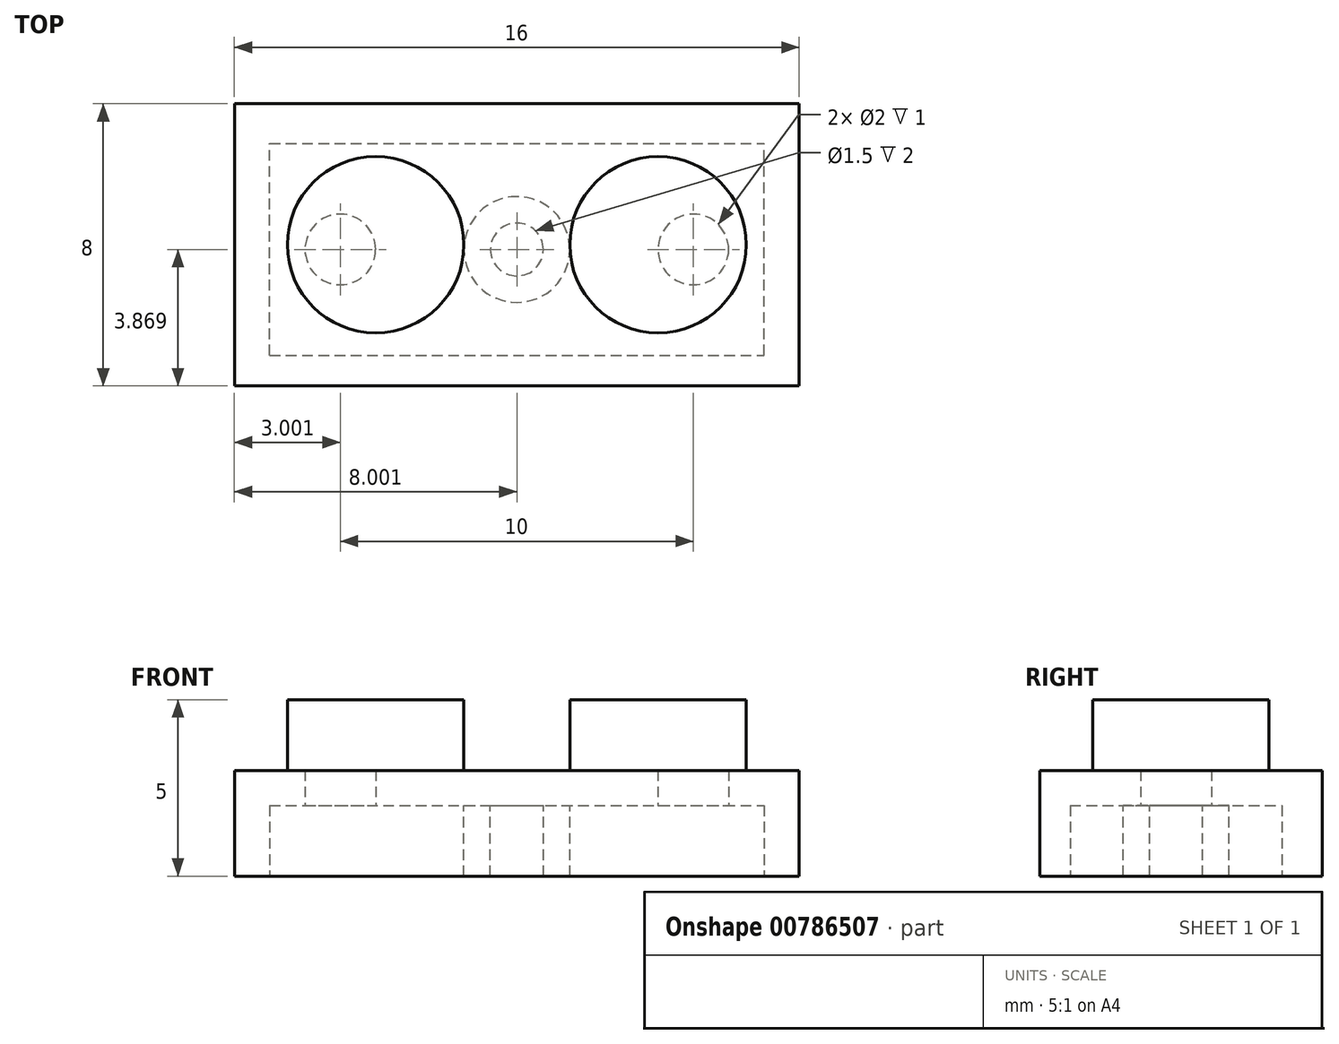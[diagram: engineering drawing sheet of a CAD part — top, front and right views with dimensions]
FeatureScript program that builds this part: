
annotation { "Feature Type Name" : "Feature", "Feature Type Description" : "" }
export const myFeature = defineFeature(function(context is Context, id is Id, definition is map)
    precondition{}
    {
        {
            var Q0;
            Q0=qCreatedBy(makeId("Top.planeOp"),FACE);
            var sketch = newSketch(context, id + "F0", { "sketchPlane" : qUnion([Q0])});
            skLineSegment(sketch, "E0.bottom", {"start": v(9.17, -1.05) * mm, "end": v(25.17, -1.05) * mm});
            skLineSegment(sketch, "E0.top", {"start": v(9.17, -9.05) * mm, "end": v(25.17, -9.05) * mm});
            skLineSegment(sketch, "E0.left", {"start": v(9.17, -1.05) * mm, "end": v(9.17, -9.05) * mm});
            skLineSegment(sketch, "E0.right", {"start": v(25.17, -1.05) * mm, "end": v(25.17, -9.05) * mm});
            skSolve(sketch);
        }
        {
            var Q0;
            Q0 = qSketchRegion(id + "F0", true);
            extrude(context, id + "F1", {"entities" : qUnion([Q0]), "depth" : 3 * mm, "offsetDistance" : 25 * mm});
        }
        {
            var Q0;
            Q0=makeQuery(id+"F1.opExtrude","CAP_FACE",FACE,{"disambiguationData":[OSD([sQuery(id+"F0.wireOp",EDGE,"E0.bottom"),sQuery(id+"F0.wireOp",EDGE,"E0.top"),sQuery(id+"F0.wireOp",EDGE,"E0.left"),sQuery(id+"F0.wireOp",EDGE,"E0.right")])],"isStart":false});
            var sketch = newSketch(context, id + "F2", { "sketchPlane" : qUnion([Q0])});
            skCircle(sketch, "E1", {"center": v(13.17, -5.05) * mm, "radius": 2.5 * mm});
            skCircle(sketch, "E2", {"center": v(21.17, -5.05) * mm, "radius": 2.5 * mm});
            skSolve(sketch);
        }
        {
            var Q0;
            Q0 = qSketchRegion(id + "F2", true);
            extrude(context, id + "F3", {"entities" : qUnion([Q0]), "operationType" : NewBodyOperationType.ADD, "depth" : 2 * mm, "offsetDistance" : 25 * mm});
        }
        {
            var Q0;
            Q0=makeQuery(id+"F1.opExtrude","CAP_FACE",FACE,{"disambiguationData":[OSD([sQuery(id+"F0.wireOp",EDGE,"E0.bottom"),sQuery(id+"F0.wireOp",EDGE,"E0.top"),sQuery(id+"F0.wireOp",EDGE,"E0.left"),sQuery(id+"F0.wireOp",EDGE,"E0.right")])],"isStart":true});
            var sketch = newSketch(context, id + "F4", { "sketchPlane" : qUnion([Q0])});
            skLineSegment(sketch, "E3.bottom", {"start": v(10.17, 8.18) * mm, "end": v(24.17, 8.18) * mm});
            skLineSegment(sketch, "E3.top", {"start": v(10.17, 2.18) * mm, "end": v(24.17, 2.18) * mm});
            skLineSegment(sketch, "E3.left", {"start": v(10.17, 8.18) * mm, "end": v(10.17, 2.18) * mm});
            skLineSegment(sketch, "E3.right", {"start": v(24.17, 8.18) * mm, "end": v(24.17, 2.18) * mm});
            skSolve(sketch);
        }
        {
            var Q0;
            Q0 = qSketchRegion(id + "F4", true);
            extrude(context, id + "F5", {"entities" : qUnion([Q0]), "operationType" : NewBodyOperationType.REMOVE, "oppositeDirection" : true, "depth" : 2 * mm, "offsetDistance" : 25 * mm});
        }
        {
            var Q0;
            Q0=makeQuery(id+"F5.boolean.opBoolean","COPY",FACE,{"derivedFrom":makeQuery(id+"F5.opExtrude","CAP_FACE",FACE,{"disambiguationData":[OSD([sQuery(id+"F4.wireOp",EDGE,"E3.bottom"),sQuery(id+"F4.wireOp",EDGE,"E3.top"),sQuery(id+"F4.wireOp",EDGE,"E3.left"),sQuery(id+"F4.wireOp",EDGE,"E3.right")])],"isStart":false})});
            var sketch = newSketch(context, id + "F6", { "sketchPlane" : qUnion([Q0])});
            skCircle(sketch, "E4", {"center": v(17.17, 5.18) * mm, "radius": 0.75 * mm});
            skPoint(sketch, "E4.centerSnap0", {"position": v(17.17, 8.18) * mm});
            skPoint(sketch, "E4.centerSnap1", {"position": v(24.17, 5.18) * mm});
            skCircle(sketch, "E5", {"center": v(17.17, 5.18) * mm, "radius": 1.5 * mm});
            skSolve(sketch);
        }
        {
            var Q0;
            Q0 = qSketchRegion(id + "F6", true);
            extrude(context, id + "F7", {"entities" : qUnion([Q0]), "operationType" : NewBodyOperationType.ADD, "depth" : 2 * mm, "offsetDistance" : 25 * mm});
        }
        {
            var Q0;
            {var subQ0=sQuery(id+"F4.wireOp",EDGE,"E3.right");var subQ1=sQuery(id+"F4.wireOp",EDGE,"E3.left");var subQ2=sQuery(id+"F4.wireOp",EDGE,"E3.top");var subQ3=sQuery(id+"F4.wireOp",EDGE,"E3.bottom");Q0=makeQuery(id+"F7.boolean.opBoolean","SPLIT",FACE,{"disambiguationData":[TD([makeQuery(id+"F5.boolean.opBoolean","COPY",FACE,{"derivedFrom":makeQuery(id+"F5.opExtrude","SWEPT_FACE",FACE,{"disambiguationData":[OSD([subQ3])]})})])],"derivedFrom":makeQuery(id+"F5.boolean.opBoolean","COPY",FACE,{"derivedFrom":makeQuery(id+"F5.opExtrude","CAP_FACE",FACE,{"disambiguationData":[OSD([subQ3,subQ2,subQ1,subQ0])],"isStart":false})})});}
            var sketch = newSketch(context, id + "F8", { "sketchPlane" : qUnion([Q0])});
            skCircle(sketch, "E6", {"center": v(12.17, 5.18) * mm, "radius": 1 * mm});
            skPoint(sketch, "E6.centerSnap0", {"position": v(10.17, 5.18) * mm});
            skCircle(sketch, "E7", {"center": v(22.17, 5.18) * mm, "radius": 1 * mm});
            skPoint(sketch, "E7.centerSnap0", {"position": v(24.17, 5.18) * mm});
            skSolve(sketch);
        }
        {
            var Q0;
            Q0 = qSketchRegion(id + "F8", true);
            extrude(context, id + "F9", {"entities" : qUnion([Q0]), "operationType" : NewBodyOperationType.REMOVE, "oppositeDirection" : true, "depth" : 1 * mm, "offsetDistance" : 25 * mm});
        }
    });
